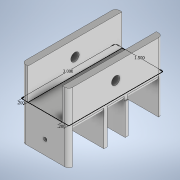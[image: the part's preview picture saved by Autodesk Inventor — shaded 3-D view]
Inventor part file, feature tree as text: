
AUTODESK INVENTOR PART (.ipt)
format: ipt  version: 2020 (Build 240168000, 168)  size: 193,536 bytes
history: native  units: in
note: dims shown in document units (in); Inventor stores cm internally (conversion verified against a paired STEP export)
features: sketch x3, extrude x3, hole x2, fillet x1
ambient origin geometry x8: Origin, YZ Plane, XZ Plane, XY Plane, X Axis, Y Axis, Z Axis, Center Point
bodies: Solid1 (feature_tree)
feature tree (9):
  sketch  "Sketch1"  dims[d0=1.5in d1=3.0in]
  extrude  "Extrusion1"  Depth=3.0in
  extrude  "Extrusion2"  Depth=0.2in
  hole  "Hole1"  [1 undecoded]
  extrude  "Extrusion3"  Depth=0.1in
  hole  "Hole2"  [1 undecoded]
  fillet  "Fillet1"  Radius=1.0in
  sketch  "Sketch2"  dims[d2=0.2in d3=0.2in]
  sketch  "Sketch3"  dims[d4=1.0in d5=0.0in d6=0.2in d7=0.0in d8=0.5in d9=0.266in d10=0.75in d11=0.438in d12=0.25in d13=0.5635in d14=1.0in d15=0.8108in d16=0.5in d17=1.0in d18=0.75in d19=0.125in d20=0.125in d21=1.0in d22=0.0in d23=0.45in d24=0.1125in d25=0.75in d26=0.438in d27=0.25in d28=0.5635in d29=1.0in d30=0.8108in d31=0.125in d32=0.125in d33=0.125in d34=1.0in d35=1.0in d36=90.0deg d37=0.1in d38=0.1in]
note: 2 required parameter values undecoded (feature->parameter linkage not recoverable at this tier; creation-order binding heuristic only, values carry confidence <= 0.55)
